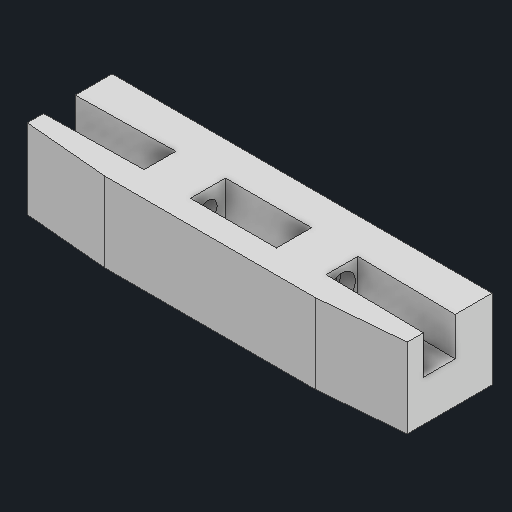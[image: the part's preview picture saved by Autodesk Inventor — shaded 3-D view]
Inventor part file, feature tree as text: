
AUTODESK INVENTOR PART (.ipt)
format: ipt  version: 2024 (Build 280153000, 153)  size: 182,272 bytes
history: native  units: in
note: dims shown in document units (in); Inventor stores cm internally (conversion verified against a paired STEP export)
features: extrude x5, sketch x5, projected_geometry x3, other x2, mirror x1, reference x1
ambient origin geometry x8: Origin, YZ Plane, XZ Plane, XY Plane, X Axis, Y Axis, Z Axis, Center Point
bodies: Solid1 (feature_tree)
feature tree (17):
  extrude  "Extrusion1"  Depth=0.37in TaperAngle=0.0deg
  extrude  "Extrusion2"  Depth=0.3937in
  extrude  "Extrusion3"  Depth=0.315in TaperAngle=0.0deg
  extrude  "Extrusion4"  Depth=0.315in TaperAngle=0.0deg
  extrude  "Extrusion5"  Depth=0.1378in TaperAngle=0.0deg
  mirror  "Mirror1"
  sketch  "Sketch1"  dims[d0=0.0157in d1=0.4606in d2=0.37in d3=0.0in]
  sketch  "Sketch2"  dims[d4=0.3937in d5=0.0in d6=0.1654in]
  projected_geometry  "Projected Loop1"
  sketch  "Sketch3"  dims[d7=0.4724in d8=0.315in d9=0.0in]
  projected_geometry  "Projected Loop2"
  sketch  "Sketch4"  dims[d10=0.1654in d11=0.315in d12=1.9695in d13=0.0in d14=0.0in]
  reference  "Reference1"
  sketch  "Sketch5"  dims[d15=0.2598in d16=0.1378in d17=0.0in]
  projected_geometry  "Projected Loop3"
  other  "Assembly2"
  other  "Emeet_Camera:1"
